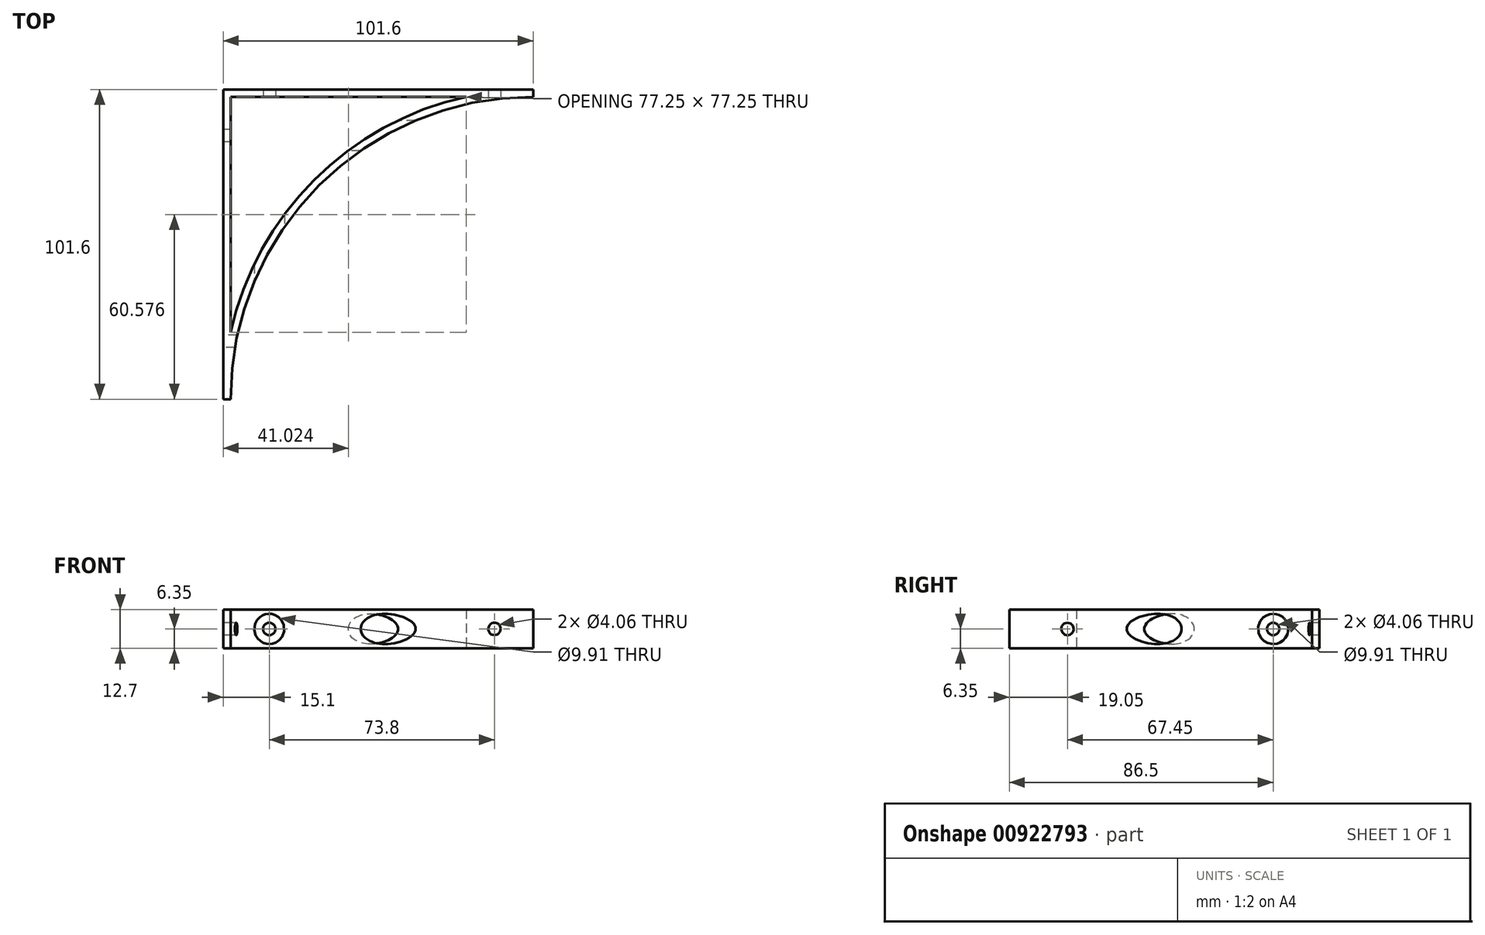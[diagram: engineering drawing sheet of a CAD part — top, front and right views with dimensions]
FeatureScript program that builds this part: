
annotation { "Feature Type Name" : "Feature", "Feature Type Description" : "" }
export const myFeature = defineFeature(function(context is Context, id is Id, definition is map)
    precondition{}
    {
        {
            var Q0;
            Q0=qCreatedBy(makeId("Top.planeOp"),FACE);
            var sketch = newSketch(context, id + "F0", { "sketchPlane" : qUnion([Q0])});
            skLineSegment(sketch, "E0", {"start": v(101.6, 101.6) * mm, "end": v(0, 101.6) * mm});
            skLineSegment(sketch, "E1", {"start": v(0, 101.6) * mm, "end": v(0, 0) * mm});
            skArc(sketch, "E2", {"start": v(79.65, 99.2) * mm, "mid": v(29.76, 71.84) * mm, "end": v(2.4, 21.95) * mm});
            skArc(sketch, "E3.0", {"start": v(101.6, 99.2) * mm, "mid": v(31.46, 70.14) * mm, "end": v(2.4, 0) * mm});
            skLineSegment(sketch, "E4", {"start": v(2.4, 0) * mm, "end": v(0, 0) * mm});
            skLineSegment(sketch, "E5", {"start": v(101.6, 101.6) * mm, "end": v(101.6, 99.2) * mm});
            skLineSegment(sketch, "E6.0", {"start": v(2.4, 99.2) * mm, "end": v(2.4, 21.95) * mm});
            skLineSegment(sketch, "E6.1", {"start": v(79.65, 99.2) * mm, "end": v(2.4, 99.2) * mm});
            skSolve(sketch);
        }
        {
            var Q0;
            Q0=makeQuery(id+"F0.imprint","IMPRINT",FACE,{"disambiguationData":[TD([[makeQuery(id+"F0.imprint","IMPRINT",EDGE,{"derivedFrom":sQuery(id+"F0.wireOp",EDGE,"E0")}),1.0]])]});
            extrude(context, id + "F1", {"entities" : qUnion([Q0]), "depth" : 12.7 * mm, "offsetDistance" : 25.4 * mm});
        }
        {
            var Q0;
            Q0=qCreatedBy(makeId("Right.planeOp"),FACE);
            var sketch = newSketch(context, id + "F2", { "sketchPlane" : qUnion([Q0])});
            skCircle(sketch, "E7", {"center": v(19.05, 6.35) * mm, "radius": 2.03 * mm});
            skCircle(sketch, "E8", {"center": v(86.5, 6.35) * mm, "radius": 2.03 * mm});
            skLineSegment(sketch, "E9", {"start": v(0, 6.35) * mm, "end": v(19.05, 6.35) * mm, "construction": true});
            skLineSegment(sketch, "E10", {"start": v(19.05, 6.35) * mm, "end": v(86.5, 6.35) * mm});
            skSolve(sketch);
        }
        {
            var Q0;
            Q0 = qSketchRegion(id + "F2", true);
            extrude(context, id + "F3", {"entities" : qUnion([Q0]), "operationType" : NewBodyOperationType.REMOVE, "endBound" : BoundingType.THROUGH_ALL, "depth" : 25.4 * mm, "offsetDistance" : 25.4 * mm});
        }
        {
            var Q0;
            Q0=qCreatedBy(makeId("Front.planeOp"),FACE);
            var sketch = newSketch(context, id + "F4", { "sketchPlane" : qUnion([Q0])});
            skCircle(sketch, "E11", {"center": v(15.1, 6.35) * mm, "radius": 2.03 * mm});
            skCircle(sketch, "E12", {"center": v(88.9, 6.35) * mm, "radius": 2.03 * mm});
            skLineSegment(sketch, "E13", {"start": v(15.1, 6.35) * mm, "end": v(88.9, 6.35) * mm, "construction": true});
            skLineSegment(sketch, "E14", {"start": v(101.6, 6.35) * mm, "end": v(88.9, 6.35) * mm, "construction": true});
            skSolve(sketch);
        }
        {
            var Q0;
            Q0=makeQuery(id+"F4.imprint","IMPRINT",FACE,{"disambiguationData":[TD([[makeQuery(id+"F4.imprint","IMPRINT",EDGE,{"derivedFrom":sQuery(id+"F4.wireOp",EDGE,"E11")}),1.0]])]});
            var Q1;
            Q1=makeQuery(id+"F4.imprint","IMPRINT",FACE,{"disambiguationData":[TD([[makeQuery(id+"F4.imprint","IMPRINT",EDGE,{"derivedFrom":sQuery(id+"F4.wireOp",EDGE,"E12")}),1.0]])]});
            extrude(context, id + "F5", {"entities" : qUnion([Q0, Q1]), "operationType" : NewBodyOperationType.REMOVE, "endBound" : BoundingType.THROUGH_ALL, "oppositeDirection" : true, "depth" : 25.4 * mm, "offsetDistance" : 25.4 * mm});
        }
        {
            var Q0;
            Q0=qCreatedBy(makeId("Front.planeOp"),FACE);
            var sketch = newSketch(context, id + "F6", { "sketchPlane" : qUnion([Q0])});
            skCircle(sketch, "E15", {"center": v(15.1, 6.35) * mm, "radius": 4.95 * mm});
            skSolve(sketch);
        }
        {
            var Q0;
            Q0 = qSketchRegion(id + "F6", true);
            extrude(context, id + "F7", {"entities" : qUnion([Q0]), "operationType" : NewBodyOperationType.REMOVE, "oppositeDirection" : true, "depth" : 63.25 * mm, "offsetDistance" : 25.4 * mm});
        }
        {
            var Q0;
            Q0=qCreatedBy(makeId("Right.planeOp"),FACE);
            var sketch = newSketch(context, id + "F8", { "sketchPlane" : qUnion([Q0])});
            skCircle(sketch, "E16", {"center": v(86.5, 6.35) * mm, "radius": 4.95 * mm});
            skSolve(sketch);
        }
        {
            var Q0;
            Q0 = qSketchRegion(id + "F8", true);
            extrude(context, id + "F9", {"entities" : qUnion([Q0]), "operationType" : NewBodyOperationType.REMOVE, "depth" : 68.07 * mm, "offsetDistance" : 25.4 * mm, "hasSecondDirection" : true, "secondDirectionOppositeDirection" : false, "secondDirectionDepth" : 18.54 * mm});
        }
    });
